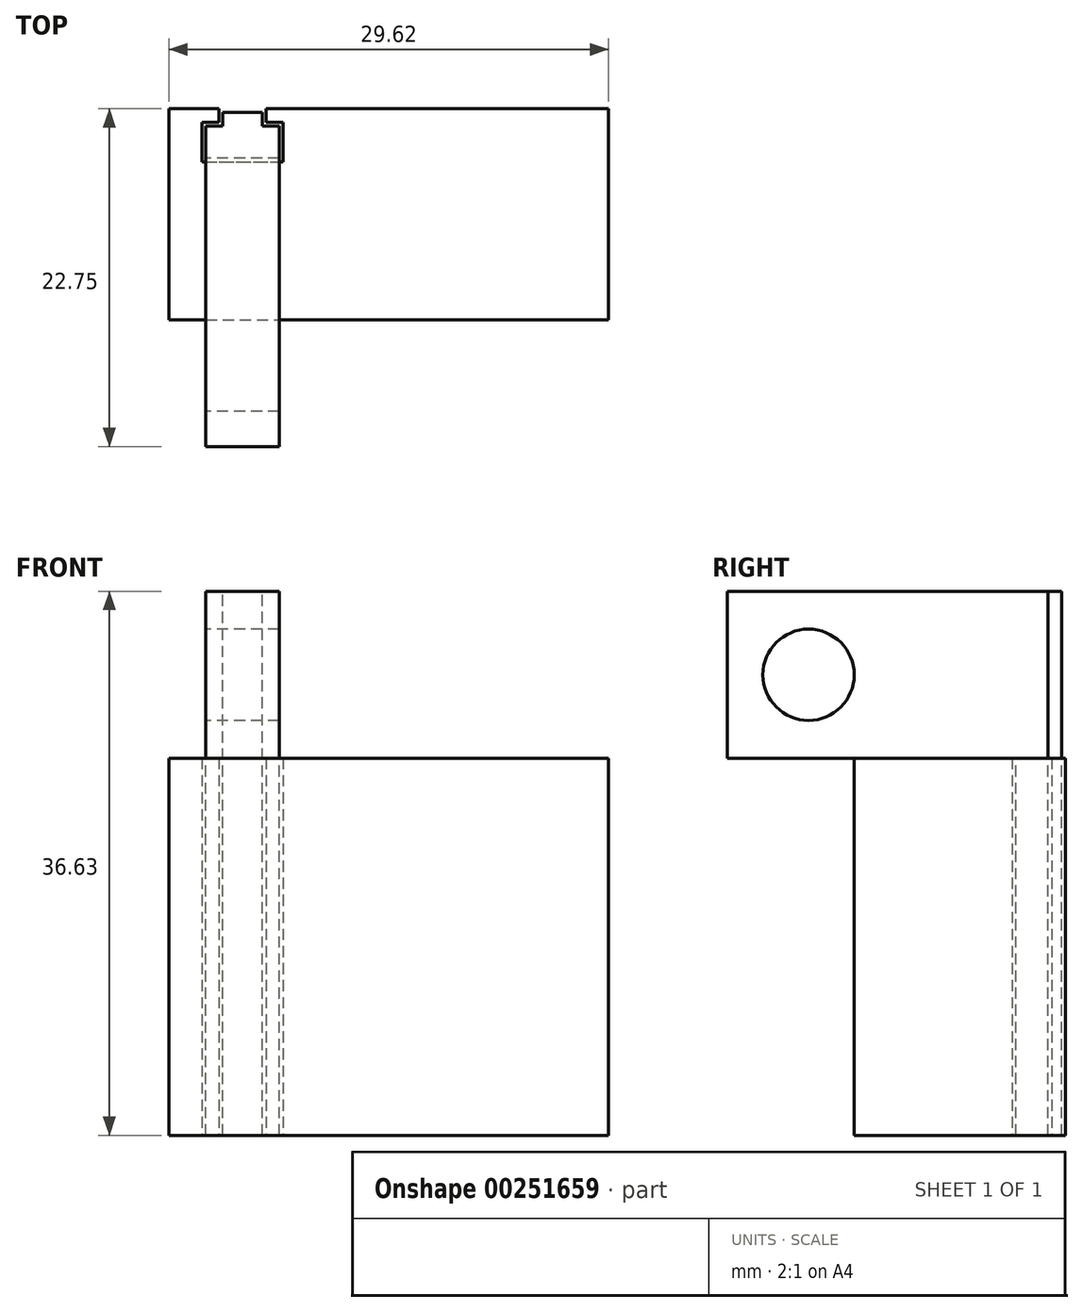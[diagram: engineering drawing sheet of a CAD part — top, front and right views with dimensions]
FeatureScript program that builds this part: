
annotation { "Feature Type Name" : "Feature", "Feature Type Description" : "" }
export const myFeature = defineFeature(function(context is Context, id is Id, definition is map)
    precondition{}
    {
        {
            var Q0;
            Q0=qCreatedBy(makeId("Top.planeOp"),FACE);
            var sketch = newSketch(context, id + "F0", { "sketchPlane" : qUnion([Q0])});
            skLineSegment(sketch, "E0.bottom", {"start": v(0, 0) * mm, "end": v(1.13, 0) * mm});
            skLineSegment(sketch, "E0.top", {"start": v(0, -2.67) * mm, "end": v(5.46, -2.67) * mm});
            skLineSegment(sketch, "E0.left", {"start": v(0, 0) * mm, "end": v(0, -2.67) * mm});
            skLineSegment(sketch, "E0.right", {"start": v(5.46, 0) * mm, "end": v(5.46, -2.67) * mm});
            skLineSegment(sketch, "E1.top", {"start": v(1.13, 0.91) * mm, "end": v(4.33, 0.91) * mm});
            skLineSegment(sketch, "E1.left", {"start": v(1.13, 0) * mm, "end": v(1.13, 0.91) * mm});
            skLineSegment(sketch, "E1.right", {"start": v(4.33, 0) * mm, "end": v(4.33, 0.91) * mm});
            skLineSegment(sketch, "E2.trimOffspring", {"start": v(4.33, 0) * mm, "end": v(5.46, 0) * mm});
            skLineSegment(sketch, "E3.bottom", {"start": v(-2.24, 0.91) * mm, "end": v(27.38, 0.91) * mm});
            skLineSegment(sketch, "E3.top", {"start": v(-2.24, -13.3) * mm, "end": v(27.38, -13.3) * mm});
            skLineSegment(sketch, "E3.left", {"start": v(-2.24, 0.91) * mm, "end": v(-2.24, -13.3) * mm});
            skLineSegment(sketch, "E3.right", {"start": v(27.38, 0.91) * mm, "end": v(27.38, -13.3) * mm});
            skSolve(sketch);
        }
        {
            var Q0;
            Q0=makeQuery(id+"F0.imprint","IMPRINT",FACE,{"disambiguationData":[TD([[makeQuery(id+"F0.imprint","IMPRINT",EDGE,{"derivedFrom":sQuery(id+"F0.wireOp",EDGE,"E0.bottom")}),1.0]])]});
            extrude(context, id + "F1", {"entities" : qUnion([Q0]), "depth" : 25.4 * mm});
        }
        {
            var Q0;
            Q0=makeQuery(id+"F1.opExtrude","CAP_FACE",FACE,{"disambiguationData":[OSD([sQuery(id+"F0.wireOp",EDGE,"E0.bottom"),sQuery(id+"F0.wireOp",EDGE,"E0.top"),sQuery(id+"F0.wireOp",EDGE,"E0.left"),sQuery(id+"F0.wireOp",EDGE,"E0.right"),sQuery(id+"F0.wireOp",EDGE,"E1.left"),sQuery(id+"F0.wireOp",EDGE,"E1.right"),sQuery(id+"F0.wireOp",EDGE,"E2.trimOffspring"),sQuery(id+"F0.wireOp",EDGE,"E3.bottom"),sQuery(id+"F0.wireOp",EDGE,"E3.top"),sQuery(id+"F0.wireOp",EDGE,"E3.left"),sQuery(id+"F0.wireOp",EDGE,"E3.right")])],"isStart":false});
            var sketch = newSketch(context, id + "F2", { "sketchPlane" : qUnion([Q0])});
            skLineSegment(sketch, "E4.0", {"start": v(0, -2.67) * mm, "end": v(5.46, -2.67) * mm, "construction": true});
            skLineSegment(sketch, "E4.1", {"start": v(5.46, 0) * mm, "end": v(5.46, -2.67) * mm, "construction": true});
            skLineSegment(sketch, "E4.2", {"start": v(4.33, 0) * mm, "end": v(5.46, 0) * mm, "construction": true});
            skLineSegment(sketch, "E4.3", {"start": v(4.33, 0) * mm, "end": v(4.33, 0.91) * mm, "construction": true});
            skLineSegment(sketch, "E4.4", {"start": v(1.13, 0) * mm, "end": v(1.13, 0.91) * mm, "construction": true});
            skLineSegment(sketch, "E4.5", {"start": v(0, 0) * mm, "end": v(1.13, 0) * mm, "construction": true});
            skLineSegment(sketch, "E4.6", {"start": v(0, 0) * mm, "end": v(0, -2.67) * mm, "construction": true});
            skLineSegment(sketch, "E5", {"start": v(1.13, 0.91) * mm, "end": v(4.33, 0.91) * mm, "construction": true});
            skLineSegment(sketch, "E6.0", {"start": v(0.25, -0.25) * mm, "end": v(1.38, -0.25) * mm});
            skLineSegment(sketch, "E6.1", {"start": v(0.25, -0.25) * mm, "end": v(0.25, -2.41) * mm});
            skLineSegment(sketch, "E6.2", {"start": v(1.38, -0.25) * mm, "end": v(1.38, 0.66) * mm});
            skLineSegment(sketch, "E6.3", {"start": v(0.25, -2.41) * mm, "end": v(5.2, -2.41) * mm});
            skLineSegment(sketch, "E6.4", {"start": v(1.38, 0.66) * mm, "end": v(4.08, 0.66) * mm});
            skLineSegment(sketch, "E6.5", {"start": v(4.08, -0.25) * mm, "end": v(4.08, 0.66) * mm});
            skLineSegment(sketch, "E6.6", {"start": v(4.08, -0.25) * mm, "end": v(5.2, -0.25) * mm});
            skLineSegment(sketch, "E6.7", {"start": v(5.2, -0.25) * mm, "end": v(5.2, -2.41) * mm});
            skSolve(sketch);
        }
        {
            var Q0;
            Q0 = qSketchRegion(id + "F2", true);
            var Q1;
            Q1 = qConstructionFilter(qBodyType(qCreatedBy(id + "F2" ,EDGE), BodyType.WIRE), ConstructionObject.NO);
            var Q2;
            Q2=makeQuery(id+"F1.opExtrude","CAP_FACE",FACE,{"disambiguationData":[OSD([sQuery(id+"F0.wireOp",EDGE,"E0.bottom"),sQuery(id+"F0.wireOp",EDGE,"E0.top"),sQuery(id+"F0.wireOp",EDGE,"E0.left"),sQuery(id+"F0.wireOp",EDGE,"E0.right"),sQuery(id+"F0.wireOp",EDGE,"E1.left"),sQuery(id+"F0.wireOp",EDGE,"E1.right"),sQuery(id+"F0.wireOp",EDGE,"E2.trimOffspring"),sQuery(id+"F0.wireOp",EDGE,"E3.bottom"),sQuery(id+"F0.wireOp",EDGE,"E3.top"),sQuery(id+"F0.wireOp",EDGE,"E3.left"),sQuery(id+"F0.wireOp",EDGE,"E3.right")])],"isStart":true});
            extrude(context, id + "F3", {"entities" : qUnion([Q0]), "surfaceEntities" : qUnion([Q1]), "endBound" : BoundingType.UP_TO_SURFACE, "oppositeDirection" : true, "endBoundEntityFace" : qUnion([Q2]), "depth" : 25.4 * mm});
        }
        {
            var Q0;
            Q0=makeQuery(id+"F3.opExtrude","CAP_FACE",FACE,{"disambiguationData":[OSD([sQuery(id+"F2.wireOp",EDGE,"E6.0"),sQuery(id+"F2.wireOp",EDGE,"E6.1"),sQuery(id+"F2.wireOp",EDGE,"E6.2"),sQuery(id+"F2.wireOp",EDGE,"E6.3"),sQuery(id+"F2.wireOp",EDGE,"E6.4"),sQuery(id+"F2.wireOp",EDGE,"E6.5"),sQuery(id+"F2.wireOp",EDGE,"E6.6"),sQuery(id+"F2.wireOp",EDGE,"E6.7")])],"isStart":true});
            var sketch = newSketch(context, id + "F4", { "sketchPlane" : qUnion([Q0])});
            skLineSegment(sketch, "E7.bottom", {"start": v(0.25, -0.25) * mm, "end": v(1.38, -0.25) * mm});
            skLineSegment(sketch, "E7.top", {"start": v(0.25, -21.84) * mm, "end": v(5.2, -21.84) * mm});
            skLineSegment(sketch, "E7.left", {"start": v(0.25, -0.25) * mm, "end": v(0.25, -21.84) * mm});
            skLineSegment(sketch, "E7.right", {"start": v(5.2, -0.25) * mm, "end": v(5.2, -21.84) * mm});
            skLineSegment(sketch, "E8.0", {"start": v(1.38, 0.66) * mm, "end": v(4.08, 0.66) * mm});
            skLineSegment(sketch, "E8.1", {"start": v(1.38, -0.25) * mm, "end": v(1.38, 0.66) * mm});
            skLineSegment(sketch, "E8.2", {"start": v(4.08, -0.25) * mm, "end": v(4.08, 0.66) * mm});
            skLineSegment(sketch, "E9.trimOffspring", {"start": v(4.08, -0.25) * mm, "end": v(5.2, -0.25) * mm});
            skSolve(sketch);
        }
        {
            var Q0;
            Q0 = qSketchRegion(id + "F4", true);
            extrude(context, id + "F5", {"entities" : qUnion([Q0]), "operationType" : NewBodyOperationType.ADD, "depth" : 11.23 * mm});
        }
        {
            var Q0;
            Q0=makeQuery(id+"F5.boolean.opBoolean","MERGE",FACE,{"derivedFrom":[makeQuery(id+"F3.opExtrude","SWEPT_FACE",FACE,{"disambiguationData":[OSD([sQuery(id+"F2.wireOp",EDGE,"E6.1")])]}),makeQuery(id+"F5.opExtrude","SWEPT_FACE",FACE,{"disambiguationData":[OSD([sQuery(id+"F4.wireOp",EDGE,"E7.left")])]})]});
            var sketch = newSketch(context, id + "F6", { "sketchPlane" : qUnion([Q0])});
            skCircle(sketch, "E10", {"center": v(16.38, 31.01) * mm, "radius": 3.07 * mm});
            skLineSegment(sketch, "E11.0", {"start": v(13.3, 25.4) * mm, "end": v(13.3, 0) * mm, "construction": true});
            skLineSegment(sketch, "E12", {"start": v(13.3, 31.01) * mm, "end": v(13.3, 19.7) * mm, "construction": true});
            skLineSegment(sketch, "E13", {"start": v(16.38, 27.94) * mm, "end": v(35.08, 27.94) * mm, "construction": true});
            skSolve(sketch);
        }
        {
            var Q0;
            Q0 = qSketchRegion(id + "F6", true);
            extrude(context, id + "F7", {"entities" : qUnion([Q0]), "operationType" : NewBodyOperationType.REMOVE, "endBound" : BoundingType.UP_TO_NEXT, "oppositeDirection" : true, "depth" : 25.4 * mm});
        }
    });
